# Revit family: QF_BOURGEAT_Satellite4G_GN12_chaud_1-1_entree325_pleine
name_source: partatom
category: Equipement spécialisé
revit_build: Autodesk Revit 2015 (Build: 20140606_1530(x64)
units: mm (PartAtom-declared; Revit-internal decimal feet)

## types (2) — shared parameters
Certification = NF hygiene alimentaire
Charge max = 120.00 kg
Consommation énergétique = 0.54Kwh/h NFD40-016
Diametre_roue = 80 mm  [stored 0.262467 ft]
Fabricant = BOURGEAT
Fréquence = 50 Hz
Hauteur hors tout = 689 mm  [stored 2.2605 ft]
Hauteur_poignee_porte_sol = 230 mm  [stored 0.754593 ft]
Hauteur_poignees_laterales = 804 mm  [stored 2.6378 ft]
Hauteur_porte = 542 mm
Hauteur_roue = 107 mm  [stored 0.35105 ft]
Indice de protection = IP25
Intensité nominale = 4 A
Largeur_porte = 497 mm
Longueur hors tout = 1109 mm  [stored 3.63845 ft]
Longueur_poignees_laterales = 665 mm  [stored 2.18176 ft]
Materiau_Poignee_porte = B_Elastomère_TPE_S
Materiau_bac = Acier inoxydable, brossé
Materiau_bandage = B_Elastomère_TPE_S
Materiau_porte = Acier inoxydable, brossé
Materiau_vitre = Verre, vitrage transparent, trempé
Nature isolant = Mousse sans PU
Phase = 2
Poids net à vide = 70.00 kg
Poignee_droite = Oui
Poignee_gauche = Non
Pos_V_IHM = 38 mm  [stored 0.124672 ft]
Profondeur hors tout = 821 mm  [stored 2.69357 ft]
Puissance électrique  = 950 W
Spécification du Fabricant = Satellite 4G
Tension = 230 V
URL catalogue = http://www.bourgeat.fr

## per-type parameters (varying)
| type | Humidification | Modèle |
| GN12_sans_humidification | Non | 843212 |
| GN12_humidification | Oui | 843312 |

note: [stored X ft] marks values corroborated as IEEE doubles in the binary element streams (Revit-internal decimal feet)
